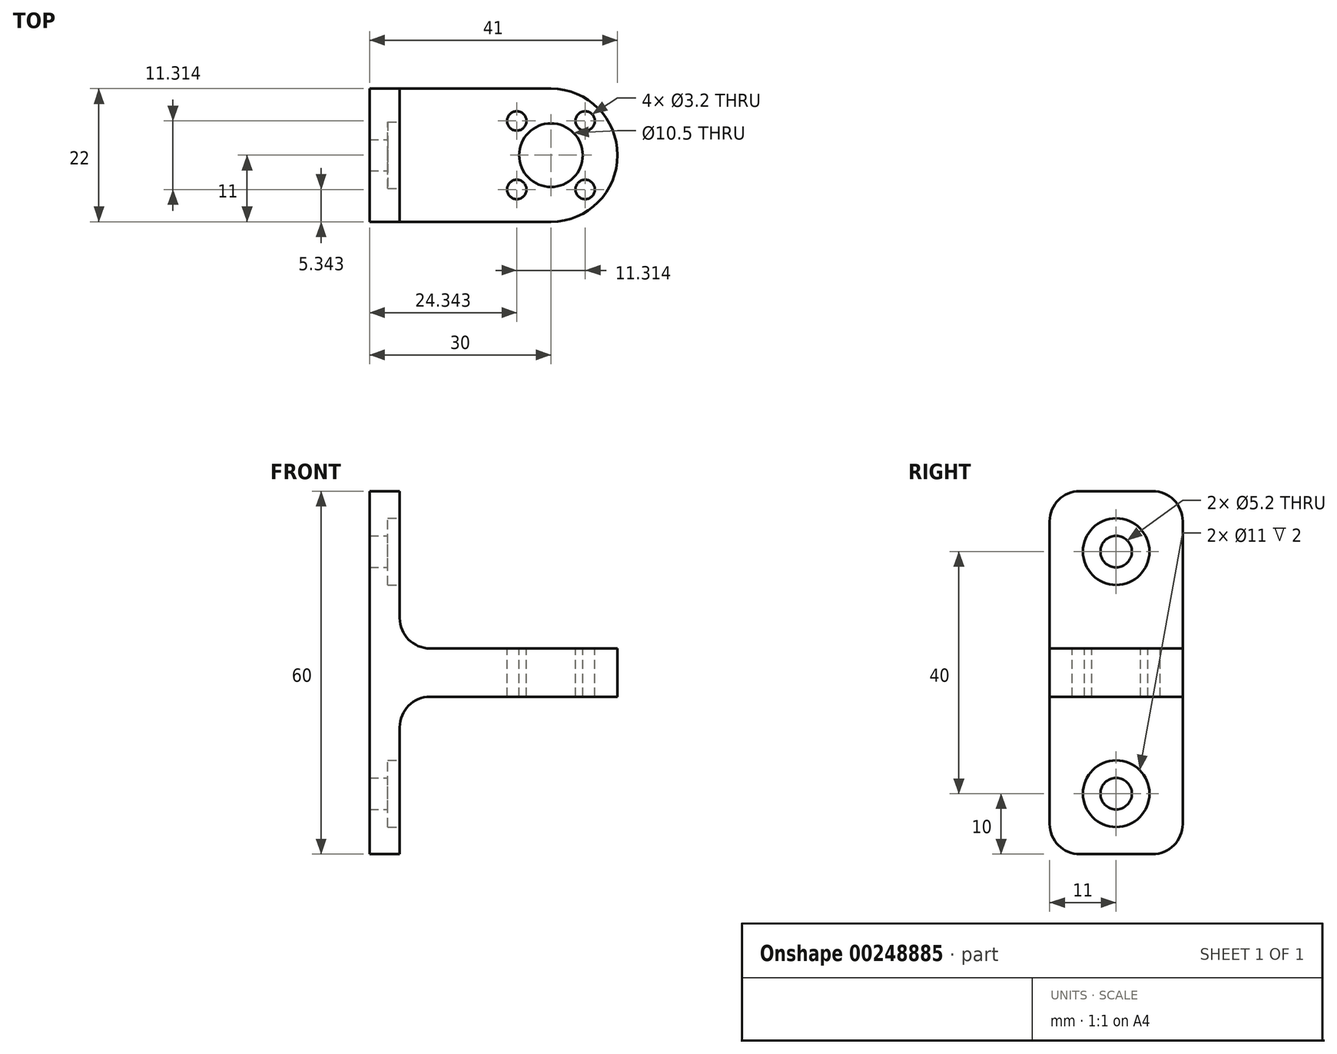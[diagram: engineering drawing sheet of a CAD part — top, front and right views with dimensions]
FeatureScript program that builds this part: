
annotation { "Feature Type Name" : "Feature", "Feature Type Description" : "" }
export const myFeature = defineFeature(function(context is Context, id is Id, definition is map)
    precondition{}
    {
        {
            var Q0;
            Q0=qCreatedBy(makeId("Right.planeOp"),FACE);
            var sketch = newSketch(context, id + "F0", { "sketchPlane" : qUnion([Q0])});
            skLineSegment(sketch, "E0", {"start": v(-120.6, 30) * mm, "end": v(120.6, 30) * mm, "construction": true});
            skLineSegment(sketch, "E1", {"start": v(-120.6, -30) * mm, "end": v(120.6, -30) * mm, "construction": true});
            skLineSegment(sketch, "E2", {"start": v(-120.6, 20) * mm, "end": v(120.6, 20) * mm, "construction": true});
            skLineSegment(sketch, "E3.0.1.0", {"start": v(-120.6, 0) * mm, "end": v(120.6, 0) * mm, "construction": true});
            skLineSegment(sketch, "E3.0.2.0", {"start": v(-120.6, -20) * mm, "end": v(120.6, -20) * mm, "construction": true});
            skLineSegment(sketch, "E3.direction1", {"start": v(-120.6, 20) * mm, "end": v(-95.6, 20) * mm, "construction": true});
            skLineSegment(sketch, "E3.direction2", {"start": v(-120.6, 20) * mm, "end": v(-120.6, 0) * mm, "construction": true});
            skPoint(sketch, "E4", {"position": v(0, 0) * mm});
            skSolve(sketch);
        }
        {
            var Q0;
            Q0=qCreatedBy(makeId("Right.planeOp"),FACE);
            var sketch = newSketch(context, id + "F1", { "sketchPlane" : qUnion([Q0])});
            skLineSegment(sketch, "E5.bottom", {"start": v(-11, 30) * mm, "end": v(11, 30) * mm});
            skLineSegment(sketch, "E5.top", {"start": v(-11, -30) * mm, "end": v(11, -30) * mm});
            skLineSegment(sketch, "E5.left", {"start": v(-11, 30) * mm, "end": v(-11, -30) * mm});
            skLineSegment(sketch, "E5.right", {"start": v(11, 30) * mm, "end": v(11, -30) * mm});
            skPoint(sketch, "E6", {"position": v(-11, 0) * mm});
            skPoint(sketch, "E7", {"position": v(0, -30) * mm});
            skLineSegment(sketch, "E8", {"start": v(-11, 4) * mm, "end": v(11, 4) * mm});
            skLineSegment(sketch, "E9.MirrorCS", {"start": v(-11, -4) * mm, "end": v(11, -4) * mm});
            skLineSegment(sketch, "E10.0", {"start": v(-120.6, 20) * mm, "end": v(120.6, 20) * mm, "construction": true});
            skLineSegment(sketch, "E11.0", {"start": v(-120.6, -20) * mm, "end": v(120.6, -20) * mm, "construction": true});
            skPoint(sketch, "E12", {"position": v(0, 20) * mm});
            skPoint(sketch, "E13", {"position": v(0, -20) * mm});
            skSolve(sketch);
        }
        {
            var Q0;
            {var subQ0=sQuery(id+"F1.wireOp",EDGE,"E5.bottom");Q0=makeQuery(id+"F1.imprint","IMPRINT",FACE,{"disambiguationData":[TD([[makeQuery(id+"F1.imprint","IMPRINT",EDGE,{"derivedFrom":subQ0}),-1.0]])]});}
            var Q1;
            {var subQ0=sQuery(id+"F1.wireOp",EDGE,"E8");Q1=makeQuery(id+"F1.imprint","IMPRINT",FACE,{"disambiguationData":[TD([[makeQuery(id+"F1.imprint","IMPRINT",EDGE,{"derivedFrom":subQ0}),-1.0]])]});}
            var Q2;
            {var subQ0=sQuery(id+"F1.wireOp",EDGE,"E5.top");Q2=makeQuery(id+"F1.imprint","IMPRINT",FACE,{"disambiguationData":[TD([[makeQuery(id+"F1.imprint","IMPRINT",EDGE,{"derivedFrom":subQ0}),1.0]])]});}
            extrude(context, id + "F2", {"entities" : qUnion([Q0, Q1, Q2]), "depth" : 5 * mm});
        }
        {
            var Q0;
            {var subQ0=sQuery(id+"F1.wireOp",EDGE,"E8");Q0=makeQuery(id+"F1.imprint","IMPRINT",FACE,{"disambiguationData":[TD([[makeQuery(id+"F1.imprint","IMPRINT",EDGE,{"derivedFrom":subQ0}),-1.0]])]});}
            extrude(context, id + "F3", {"entities" : qUnion([Q0]), "operationType" : NewBodyOperationType.ADD, "depth" : 41 * mm});
        }
        {
            var Q0;
            Q0=makeQuery(id+"F3.opExtrude","SWEPT_FACE",FACE,{"disambiguationData":[OSD([sQuery(id+"F1.wireOp",EDGE,"E8")])]});
            var sketch = newSketch(context, id + "F4", { "sketchPlane" : qUnion([Q0])});
            skLineSegment(sketch, "E14.0", {"start": v(41, -11) * mm, "end": v(41, 11) * mm, "construction": true});
            skPoint(sketch, "E15", {"position": v(30, 0) * mm});
            skPoint(sketch, "E15.positionSnap0", {"position": v(41, 0) * mm});
            skCircle(sketch, "E16", {"center": v(30, 0) * mm, "radius": 11 * mm, "construction": true});
            skCircle(sketch, "E17", {"center": v(30, 0) * mm, "radius": 8 * mm, "construction": true});
            skLineSegment(sketch, "E18", {"start": v(41, 11) * mm, "end": v(19, -11) * mm, "construction": true});
            skLineSegment(sketch, "E19", {"start": v(41, -11) * mm, "end": v(19, 11) * mm, "construction": true});
            skPoint(sketch, "E20", {"position": v(24.34, 5.66) * mm});
            skPoint(sketch, "E21", {"position": v(35.66, 5.66) * mm});
            skPoint(sketch, "E22", {"position": v(35.66, -5.66) * mm});
            skPoint(sketch, "E23", {"position": v(24.34, -5.66) * mm});
            skSolve(sketch);
        }
        {
            var Q0;
            Q0=sQuery(id+"F4.wireOp",VERTEX,"E15");
            var Q1;
            Q1=makeQuery(id+"F2.opExtrude","SWEPT_BODY",BODY,{"disambiguationData":[OSD([sQuery(id+"F1.wireOp",EDGE,"E5.bottom"),sQuery(id+"F1.wireOp",EDGE,"E5.top"),sQuery(id+"F1.wireOp",EDGE,"E5.left"),sQuery(id+"F1.wireOp",EDGE,"E5.right")])]});
            hole(context, id + "F5", {"style" : HoleStyle.SIMPLE, "endStyle" : HoleEndStyle.THROUGH, "holeDiameter" : 10.5 * mm, "tappedDepth" : 12 * mm, "tapClearance" : 3, "locations" : qUnion([Q0]), "scope" : qUnion([Q1])});
        }
        {
            var Q0;
            Q0=sQuery(id+"F4.wireOp",VERTEX,"E23");
            var Q1;
            Q1=sQuery(id+"F4.wireOp",VERTEX,"E20");
            var Q2;
            Q2=sQuery(id+"F4.wireOp",VERTEX,"E21");
            var Q3;
            Q3=sQuery(id+"F4.wireOp",VERTEX,"E22");
            var Q4;
            Q4=makeQuery(id+"F2.opExtrude","SWEPT_BODY",BODY,{"disambiguationData":[OSD([sQuery(id+"F1.wireOp",EDGE,"E5.bottom"),sQuery(id+"F1.wireOp",EDGE,"E5.top"),sQuery(id+"F1.wireOp",EDGE,"E5.left"),sQuery(id+"F1.wireOp",EDGE,"E5.right")])]});
            hole(context, id + "F6", {"style" : HoleStyle.SIMPLE, "endStyle" : HoleEndStyle.THROUGH, "holeDiameter" : 3.2 * mm, "tappedDepth" : 12 * mm, "tapClearance" : 3, "locations" : qUnion([Q0, Q1, Q2, Q3]), "scope" : qUnion([Q4])});
        }
        {
            var Q0;
            Q0=makeQuery(id+"F3.opExtrude","CAP_EDGE",EDGE,{"disambiguationData":[OSD([sQuery(id+"F1.wireOp",EDGE,"E5.right")])],"isStart":false});
            var Q1;
            Q1=makeQuery(id+"F3.opExtrude","CAP_EDGE",EDGE,{"disambiguationData":[OSD([sQuery(id+"F1.wireOp",EDGE,"E5.left")])],"isStart":false});
            fillet(context, id + "F7", {"entities" : qUnion([Q0, Q1]), "radius" : 11 * mm, "tangentPropagation" : true, "allowEdgeOverflow" : false});
        }
        {
            var Q0;
            Q0=makeQuery(id+"F3.boolean.opBoolean","INTERSECT",EDGE,{"derivedFrom":[makeQuery(id+"F2.opExtrude","CAP_FACE",FACE,{"disambiguationData":[OSD([sQuery(id+"F1.wireOp",EDGE,"E5.bottom"),sQuery(id+"F1.wireOp",EDGE,"E5.top"),sQuery(id+"F1.wireOp",EDGE,"E5.left"),sQuery(id+"F1.wireOp",EDGE,"E5.right")])],"isStart":false}),makeQuery(id+"F3.opExtrude","SWEPT_FACE",FACE,{"disambiguationData":[OSD([sQuery(id+"F1.wireOp",EDGE,"E8")])]})]});
            var Q1;
            Q1=makeQuery(id+"F3.boolean.opBoolean","INTERSECT",EDGE,{"derivedFrom":[makeQuery(id+"F2.opExtrude","CAP_FACE",FACE,{"disambiguationData":[OSD([sQuery(id+"F1.wireOp",EDGE,"E5.bottom"),sQuery(id+"F1.wireOp",EDGE,"E5.top"),sQuery(id+"F1.wireOp",EDGE,"E5.left"),sQuery(id+"F1.wireOp",EDGE,"E5.right")])],"isStart":false}),makeQuery(id+"F3.opExtrude","SWEPT_FACE",FACE,{"disambiguationData":[OSD([sQuery(id+"F1.wireOp",EDGE,"E9.MirrorCS")])]})]});
            fillet(context, id + "F8", {"entities" : qUnion([Q0, Q1]), "radius" : 5 * mm, "tangentPropagation" : true, "allowEdgeOverflow" : false});
        }
        {
            var Q0;
            {var subQ0=sQuery(id+"F1.wireOp",EDGE,"E5.left");var subQ1=sQuery(id+"F1.wireOp",EDGE,"E5.right");var subQ2=sQuery(id+"F1.wireOp",EDGE,"E5.bottom");Q0=makeQuery(id+"F3.boolean.opBoolean","SPLIT",FACE,{"disambiguationData":[TD([makeQuery(id+"F2.opExtrude","SWEPT_FACE",FACE,{"disambiguationData":[OSD([subQ2])]})])],"derivedFrom":makeQuery(id+"F2.opExtrude","CAP_FACE",FACE,{"disambiguationData":[OSD([subQ2,sQuery(id+"F1.wireOp",EDGE,"E5.top"),subQ0,subQ1])],"isStart":false})});}
            var sketch = newSketch(context, id + "F9", { "sketchPlane" : qUnion([Q0])});
            skLineSegment(sketch, "E24.0", {"start": v(-120.6, 20) * mm, "end": v(120.6, 20) * mm, "construction": true});
            skLineSegment(sketch, "E25.0", {"start": v(-120.6, -20) * mm, "end": v(120.6, -20) * mm, "construction": true});
            skPoint(sketch, "E26", {"position": v(0, 20) * mm});
            skPoint(sketch, "E27", {"position": v(0, -20) * mm});
            skSolve(sketch);
        }
        {
            var Q0;
            Q0=sQuery(id+"F9.wireOp",VERTEX,"E26");
            var Q1;
            Q1=sQuery(id+"F9.wireOp",VERTEX,"E27");
            var Q2;
            Q2=makeQuery(id+"F2.opExtrude","SWEPT_BODY",BODY,{"disambiguationData":[OSD([sQuery(id+"F1.wireOp",EDGE,"E5.bottom"),sQuery(id+"F1.wireOp",EDGE,"E5.top"),sQuery(id+"F1.wireOp",EDGE,"E5.left"),sQuery(id+"F1.wireOp",EDGE,"E5.right")])]});
            hole(context, id + "F10", {"style" : HoleStyle.C_BORE, "endStyle" : HoleEndStyle.THROUGH, "holeDiameter" : 5.2 * mm, "cBoreDiameter" : 11 * mm, "cBoreDepth" : 2 * mm, "tappedDepth" : 12 * mm, "tapClearance" : 3, "locations" : qUnion([Q0, Q1]), "scope" : qUnion([Q2])});
        }
        {
            var Q0;
            Q0=makeQuery(id+"F2.opExtrude","SWEPT_EDGE",EDGE,{"disambiguationData":[OSD([sQuery(id+"F1.wireOp",EDGE,"E5.bottom"),sQuery(id+"F1.wireOp",EDGE,"E5.left")])]});
            var Q1;
            Q1=makeQuery(id+"F2.opExtrude","SWEPT_EDGE",EDGE,{"disambiguationData":[OSD([sQuery(id+"F1.wireOp",EDGE,"E5.bottom"),sQuery(id+"F1.wireOp",EDGE,"E5.right")])]});
            var Q2;
            Q2=makeQuery(id+"F2.opExtrude","SWEPT_EDGE",EDGE,{"disambiguationData":[OSD([sQuery(id+"F1.wireOp",EDGE,"E5.top"),sQuery(id+"F1.wireOp",EDGE,"E5.left")])]});
            var Q3;
            Q3=makeQuery(id+"F2.opExtrude","SWEPT_EDGE",EDGE,{"disambiguationData":[OSD([sQuery(id+"F1.wireOp",EDGE,"E5.top"),sQuery(id+"F1.wireOp",EDGE,"E5.right")])]});
            fillet(context, id + "F11", {"entities" : qUnion([Q0, Q1, Q2, Q3]), "radius" : 5 * mm, "tangentPropagation" : true, "allowEdgeOverflow" : false});
        }
    });
